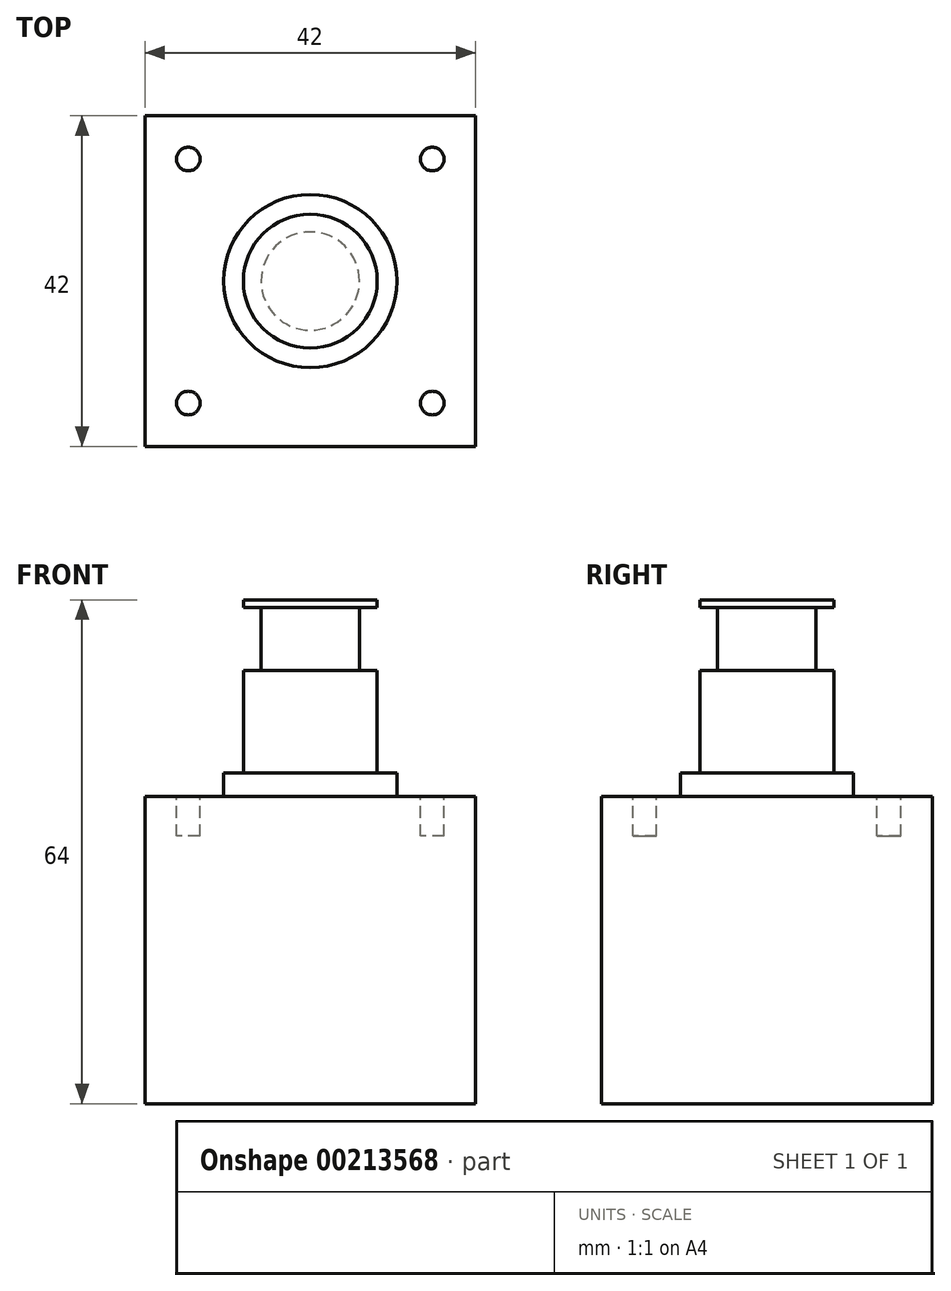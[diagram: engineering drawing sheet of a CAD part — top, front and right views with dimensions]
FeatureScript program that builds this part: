
annotation { "Feature Type Name" : "Feature", "Feature Type Description" : "" }
export const myFeature = defineFeature(function(context is Context, id is Id, definition is map)
    precondition{}
    {
        {
            var Q0;
            Q0=qCreatedBy(makeId("Top.planeOp"),FACE);
            var sketch = newSketch(context, id + "F0", { "sketchPlane" : qUnion([Q0])});
            skLineSegment(sketch, "E0.bottom", {"start": v(21, 21) * mm, "end": v(-21, 21) * mm});
            skLineSegment(sketch, "E0.top", {"start": v(21, -21) * mm, "end": v(-21, -21) * mm});
            skLineSegment(sketch, "E0.left", {"start": v(21, 21) * mm, "end": v(21, -21) * mm});
            skLineSegment(sketch, "E0.right", {"start": v(-21, 21) * mm, "end": v(-21, -21) * mm});
            skPoint(sketch, "E0.middle", {"position": v(0, 0) * mm});
            skSolve(sketch);
        }
        {
            var Q0;
            Q0 = qSketchRegion(id + "F0", true);
            extrude(context, id + "F1", {"entities" : qUnion([Q0]), "depth" : 39 * mm});
        }
        {
            var Q0;
            Q0=makeQuery(id+"F1.opExtrude","CAP_FACE",FACE,{"disambiguationData":[OSD([sQuery(id+"F0.wireOp",EDGE,"E0.bottom"),sQuery(id+"F0.wireOp",EDGE,"E0.top"),sQuery(id+"F0.wireOp",EDGE,"E0.left"),sQuery(id+"F0.wireOp",EDGE,"E0.right")])],"isStart":false});
            var sketch = newSketch(context, id + "F2", { "sketchPlane" : qUnion([Q0])});
            skCircle(sketch, "E1", {"center": v(0, 0) * mm, "radius": 11 * mm});
            skSolve(sketch);
        }
        {
            var Q0;
            Q0 = qSketchRegion(id + "F2", true);
            extrude(context, id + "F3", {"entities" : qUnion([Q0]), "operationType" : NewBodyOperationType.ADD, "depth" : 3 * mm});
        }
        {
            var Q0;
            Q0=makeQuery(id+"F1.opExtrude","CAP_FACE",FACE,{"disambiguationData":[OSD([sQuery(id+"F0.wireOp",EDGE,"E0.bottom"),sQuery(id+"F0.wireOp",EDGE,"E0.top"),sQuery(id+"F0.wireOp",EDGE,"E0.left"),sQuery(id+"F0.wireOp",EDGE,"E0.right")])],"isStart":false});
            var sketch = newSketch(context, id + "F4", { "sketchPlane" : qUnion([Q0])});
            skCircle(sketch, "E2", {"center": v(-15.5, 15.5) * mm, "radius": 1.5 * mm});
            skCircle(sketch, "E3", {"center": v(15.5, 15.5) * mm, "radius": 1.5 * mm});
            skCircle(sketch, "E4", {"center": v(15.5, -15.5) * mm, "radius": 1.5 * mm});
            skCircle(sketch, "E5", {"center": v(-15.5, -15.5) * mm, "radius": 1.5 * mm});
            skSolve(sketch);
        }
        {
            var Q0;
            Q0 = qSketchRegion(id + "F4", true);
            extrude(context, id + "F5", {"entities" : qUnion([Q0]), "operationType" : NewBodyOperationType.REMOVE, "oppositeDirection" : true, "depth" : 5 * mm});
        }
        {
            var Q0;
            Q0=makeQuery(id+"F3.opExtrude","CAP_FACE",FACE,{"disambiguationData":[OSD([sQuery(id+"F2.wireOp",EDGE,"E1")])],"isStart":false});
            var sketch = newSketch(context, id + "F6", { "sketchPlane" : qUnion([Q0])});
            skCircle(sketch, "E6", {"center": v(0, 0) * mm, "radius": 8.5 * mm});
            skSolve(sketch);
        }
        {
            var Q0;
            Q0 = qSketchRegion(id + "F6", true);
            extrude(context, id + "F7", {"entities" : qUnion([Q0]), "depth" : 22 * mm});
        }
        {
            var Q0;
            Q0=makeQuery(id+"F7.opExtrude","CAP_FACE",FACE,{"disambiguationData":[OSD([sQuery(id+"F6.wireOp",EDGE,"E6")])],"isStart":false});
            var sketch = newSketch(context, id + "F8", { "sketchPlane" : qUnion([Q0])});
            skCircle(sketch, "E7", {"center": v(0, 0) * mm, "radius": 6.25 * mm});
            skCircle(sketch, "E8", {"center": v(0, 0) * mm, "radius": 31.18 * mm});
            skSolve(sketch);
        }
        {
            var Q0;
            Q0 = qSketchRegion(id + "F8", true);
            extrude(context, id + "F9", {"entities" : qUnion([Q0]), "operationType" : NewBodyOperationType.REMOVE, "oppositeDirection" : true, "depth" : 9 * mm});
        }
        {
            var Q0;
            Q0=makeQuery(id+"F7.opExtrude","CAP_FACE",FACE,{"disambiguationData":[OSD([sQuery(id+"F6.wireOp",EDGE,"E6")])],"isStart":false});
            var sketch = newSketch(context, id + "F10", { "sketchPlane" : qUnion([Q0])});
            skCircle(sketch, "E9", {"center": v(0, 0) * mm, "radius": 8.5 * mm});
            skSolve(sketch);
        }
        {
            var Q0;
            Q0 = qSketchRegion(id + "F10", true);
            extrude(context, id + "F11", {"entities" : qUnion([Q0]), "operationType" : NewBodyOperationType.ADD, "oppositeDirection" : true, "depth" : 1 * mm});
        }
    });
